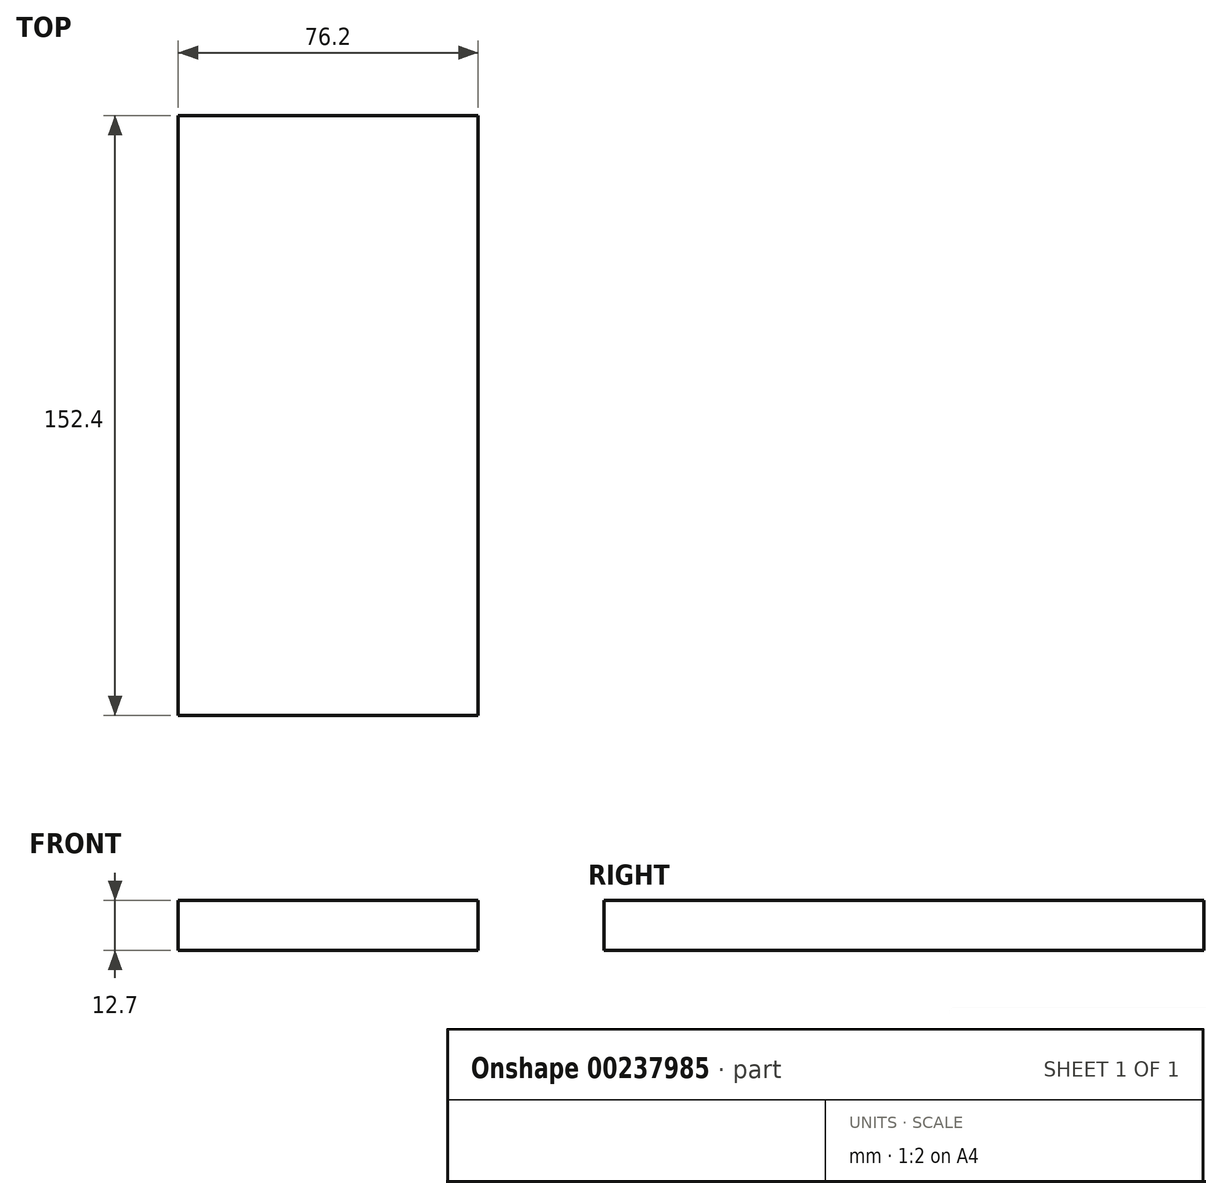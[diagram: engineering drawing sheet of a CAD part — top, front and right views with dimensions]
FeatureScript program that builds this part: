
annotation { "Feature Type Name" : "Feature", "Feature Type Description" : "" }
export const myFeature = defineFeature(function(context is Context, id is Id, definition is map)
    precondition{}
    {
        {
            var Q0;
            Q0=qCreatedBy(makeId("Top.planeOp"),FACE);
            var sketch = newSketch(context, id + "F0", { "sketchPlane" : qUnion([Q0])});
            skLineSegment(sketch, "E0.bottom", {"start": v(38.1, 76.2) * mm, "end": v(-38.1, 76.2) * mm});
            skLineSegment(sketch, "E0.top", {"start": v(38.1, -76.2) * mm, "end": v(-38.1, -76.2) * mm});
            skLineSegment(sketch, "E0.left", {"start": v(38.1, 76.2) * mm, "end": v(38.1, -76.2) * mm});
            skLineSegment(sketch, "E0.right", {"start": v(-38.1, 76.2) * mm, "end": v(-38.1, -76.2) * mm});
            skPoint(sketch, "E0.middle", {"position": v(0, 0) * mm});
            skSolve(sketch);
        }
        {
            var Q0;
            Q0 = qSketchRegion(id + "F0", true);
            extrude(context, id + "F1", {"entities" : qUnion([Q0]), "depth" : 12.7 * mm});
        }
    });
